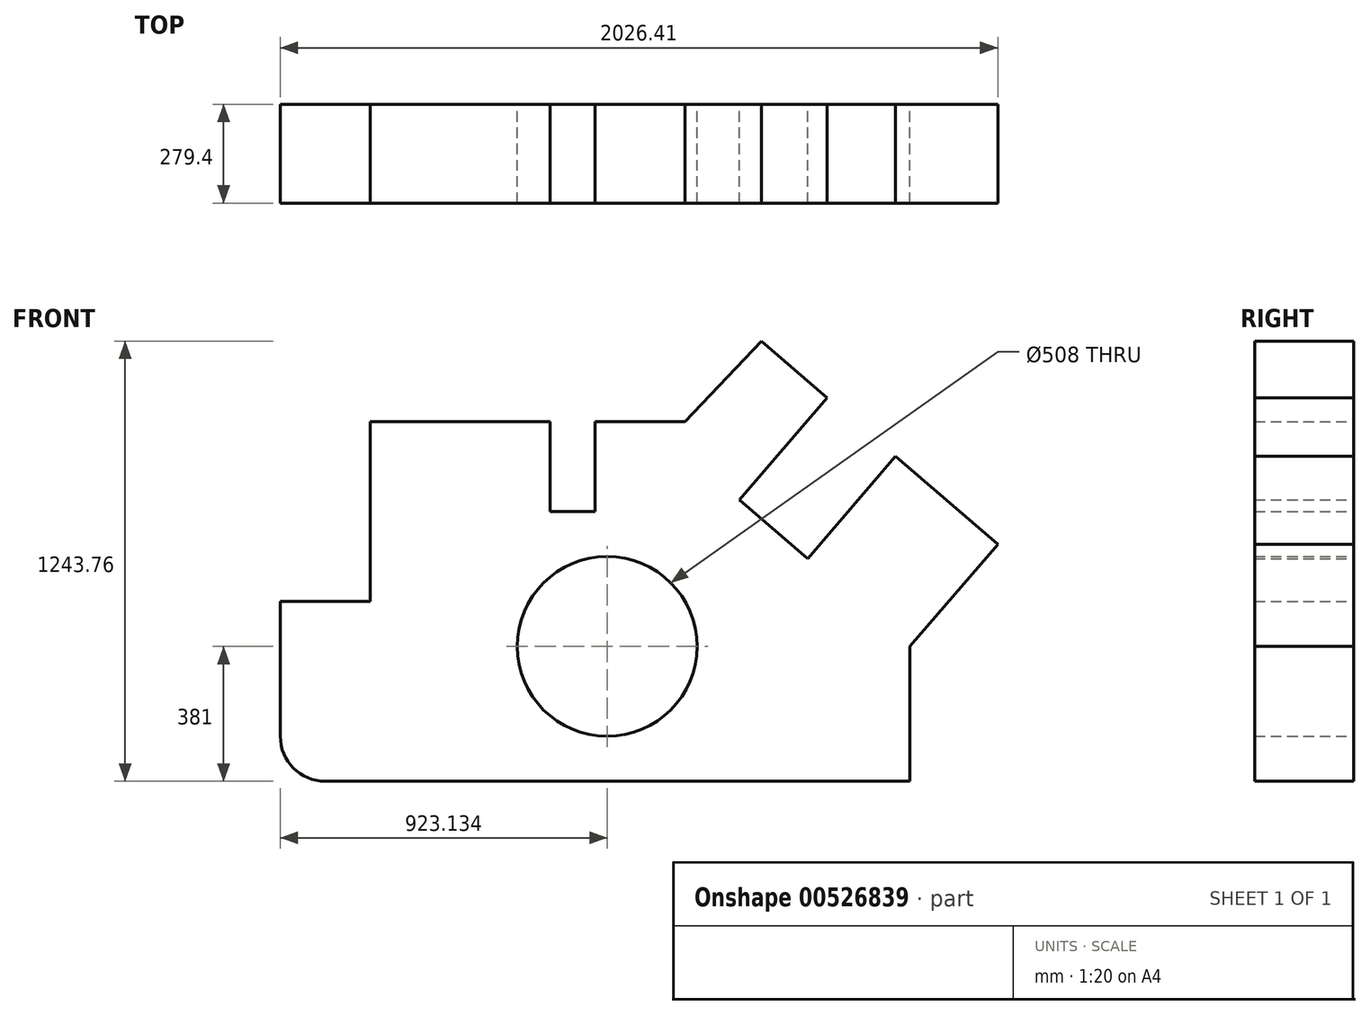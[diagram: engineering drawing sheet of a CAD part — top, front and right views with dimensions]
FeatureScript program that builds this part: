
annotation { "Feature Type Name" : "Feature", "Feature Type Description" : "" }
export const myFeature = defineFeature(function(context is Context, id is Id, definition is map)
    precondition{}
    {
        {
            var Q0;
            Q0=qCreatedBy(makeId("Front.planeOp"),FACE);
            var sketch = newSketch(context, id + "F0", { "sketchPlane" : qUnion([Q0])});
            skLineSegment(sketch, "E0", {"start": v(1778, 0) * mm, "end": v(1778, 381) * mm});
            skLineSegment(sketch, "E1", {"start": v(0, 127) * mm, "end": v(0, 508) * mm});
            skPoint(sketch, "E2.visualSharp", {"position": v(0, 0) * mm});
            skArc(sketch, "E2.filletArc", {"start": v(0, 127) * mm, "mid": v(37.2, 37.2) * mm, "end": v(127, 0) * mm});
            skCircle(sketch, "E3", {"center": v(923.13, 381) * mm, "radius": 254 * mm});
            skLineSegment(sketch, "E4", {"start": v(0, 508) * mm, "end": v(254, 508) * mm});
            skLineSegment(sketch, "E5", {"start": v(254, 508) * mm, "end": v(254, 1016) * mm});
            skLineSegment(sketch, "E6", {"start": v(254, 1016) * mm, "end": v(762, 1016) * mm});
            skLineSegment(sketch, "E7", {"start": v(762, 1016) * mm, "end": v(762, 762) * mm});
            skLineSegment(sketch, "E8", {"start": v(762, 762) * mm, "end": v(889, 762) * mm});
            skLineSegment(sketch, "E9", {"start": v(889, 762) * mm, "end": v(889, 1016) * mm});
            skLineSegment(sketch, "E10", {"start": v(889, 1016) * mm, "end": v(1143, 1016) * mm});
            skLineSegment(sketch, "E11", {"start": v(1778, 381) * mm, "end": v(2026.4, 669.89) * mm});
            skLineSegment(sketch, "E12", {"start": v(2026.4, 669.89) * mm, "end": v(1737.52, 918.3) * mm});
            skLineSegment(sketch, "E13", {"start": v(1737.52, 918.3) * mm, "end": v(1489.11, 629.4) * mm});
            skLineSegment(sketch, "E14", {"start": v(1489.11, 629.4) * mm, "end": v(1296.52, 795.01) * mm});
            skLineSegment(sketch, "E15", {"start": v(1296.52, 795.01) * mm, "end": v(1544.93, 1083.9) * mm});
            skLineSegment(sketch, "E16", {"start": v(1544.93, 1083.9) * mm, "end": v(1359.02, 1243.76) * mm});
            skLineSegment(sketch, "E17", {"start": v(1359.02, 1243.76) * mm, "end": v(1143, 1016) * mm});
            skLineSegment(sketch, "E18", {"start": v(127, 0) * mm, "end": v(1778, 0) * mm});
            skSolve(sketch);
        }
        {
            var Q0;
            Q0 = qSketchRegion(id + "F0", true);
            extrude(context, id + "F1", {"entities" : qUnion([Q0]), "depth" : 25.4 * mm, "offsetDistance" : 25.4 * mm});
        }
        {
            var Q0;
            Q0 = qSketchRegion(id + "F0", true);
            var Q1;
            Q1=makeQuery(id+"F1.opExtrude","CAP_FACE",FACE,{"disambiguationData":[OSD([sQuery(id+"F0.wireOp",EDGE,"E0"),sQuery(id+"F0.wireOp",EDGE,"E1"),sQuery(id+"F0.wireOp",EDGE,"E2.filletArc"),sQuery(id+"F0.wireOp",EDGE,"E3"),sQuery(id+"F0.wireOp",EDGE,"E4"),sQuery(id+"F0.wireOp",EDGE,"E5"),sQuery(id+"F0.wireOp",EDGE,"E6"),sQuery(id+"F0.wireOp",EDGE,"E7"),sQuery(id+"F0.wireOp",EDGE,"E8"),sQuery(id+"F0.wireOp",EDGE,"E9"),sQuery(id+"F0.wireOp",EDGE,"E10"),sQuery(id+"F0.wireOp",EDGE,"E11"),sQuery(id+"F0.wireOp",EDGE,"E12"),sQuery(id+"F0.wireOp",EDGE,"E13"),sQuery(id+"F0.wireOp",EDGE,"E14"),sQuery(id+"F0.wireOp",EDGE,"E15"),sQuery(id+"F0.wireOp",EDGE,"E16"),sQuery(id+"F0.wireOp",EDGE,"E17"),sQuery(id+"F0.wireOp",EDGE,"E18")])],"isStart":false});
            extrude(context, id + "F2", {"entities" : qUnion([Q0, Q1]), "operationType" : NewBodyOperationType.ADD, "depth" : 254 * mm, "offsetDistance" : 25.4 * mm});
        }
    });
